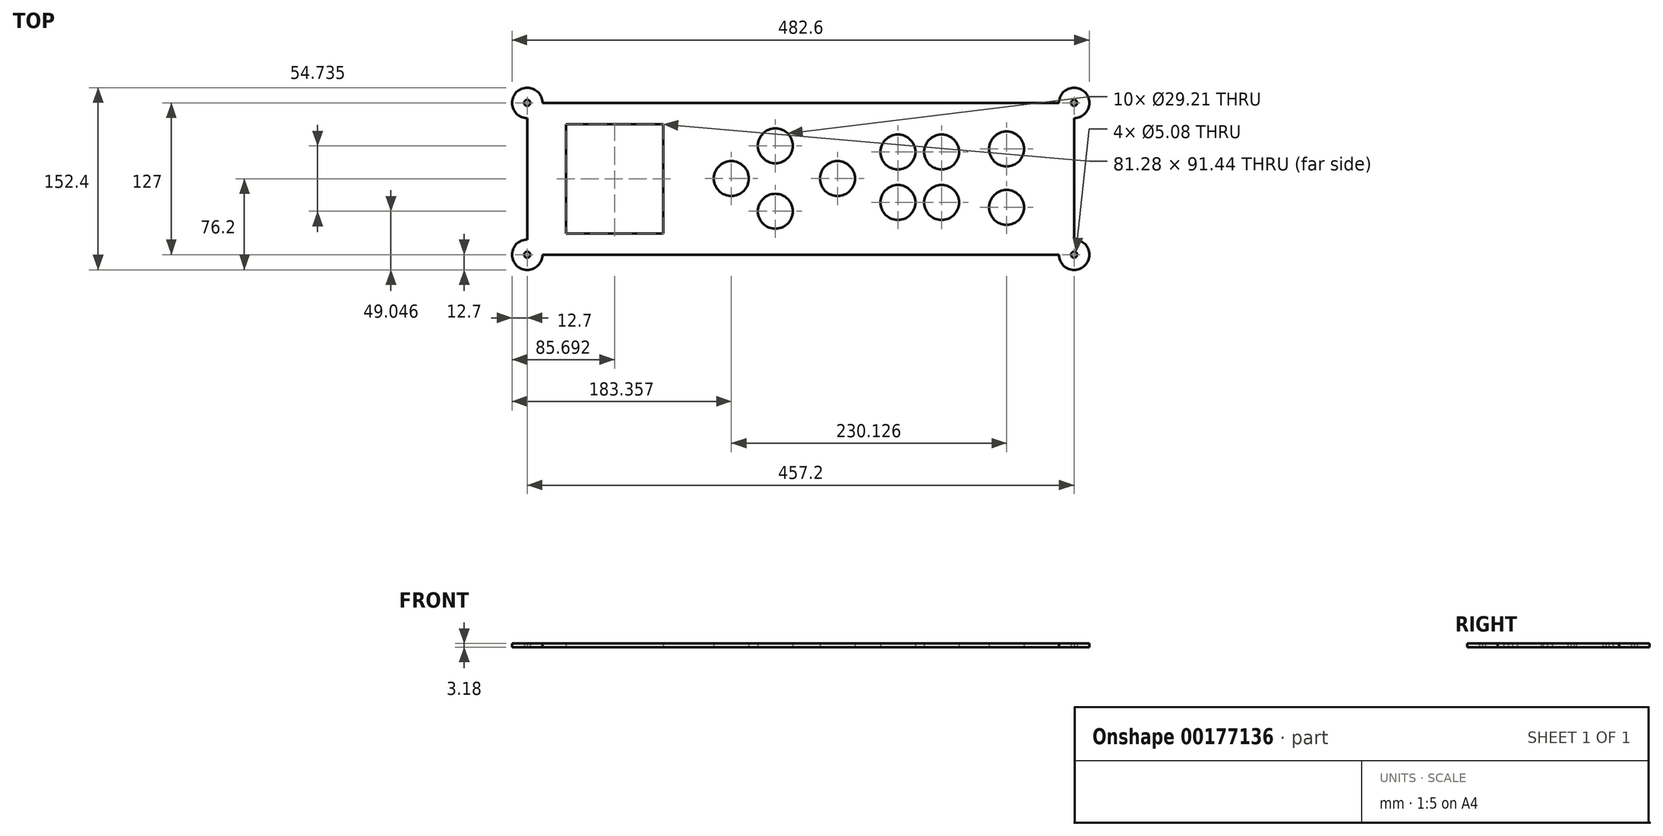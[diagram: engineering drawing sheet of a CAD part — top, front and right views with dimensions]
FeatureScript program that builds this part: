
annotation { "Feature Type Name" : "Feature", "Feature Type Description" : "" }
export const myFeature = defineFeature(function(context is Context, id is Id, definition is map)
    precondition{}
    {
        {
            var Q0;
            Q0=qCreatedBy(makeId("Top.planeOp"),FACE);
            var sketch = newSketch(context, id + "F0", { "sketchPlane" : qUnion([Q0])});
            skLineSegment(sketch, "E0.bottom", {"start": v(12.7, 0) * mm, "end": v(444.5, 0) * mm});
            skLineSegment(sketch, "E0.top", {"start": v(12.7, 127) * mm, "end": v(444.5, 127) * mm});
            skLineSegment(sketch, "E0.left", {"start": v(0, 12.7) * mm, "end": v(0, 114.3) * mm});
            skLineSegment(sketch, "E0.right", {"start": v(457.2, 12.7) * mm, "end": v(457.2, 114.3) * mm});
            skLineSegment(sketch, "E1.bottom", {"start": v(32.35, 109.22) * mm, "end": v(113.63, 109.22) * mm});
            skLineSegment(sketch, "E1.top", {"start": v(32.35, 17.78) * mm, "end": v(113.63, 17.78) * mm});
            skLineSegment(sketch, "E1.left", {"start": v(32.35, 109.22) * mm, "end": v(32.35, 17.78) * mm});
            skLineSegment(sketch, "E1.right", {"start": v(113.63, 109.22) * mm, "end": v(113.63, 17.78) * mm});
            skCircle(sketch, "E2", {"center": v(207.43, 91.08) * mm, "radius": 14.6 * mm});
            skCircle(sketch, "E3", {"center": v(207.43, 36.35) * mm, "radius": 14.6 * mm});
            skCircle(sketch, "E4", {"center": v(170.66, 63.71) * mm, "radius": 14.6 * mm});
            skCircle(sketch, "E5", {"center": v(259.47, 63.71) * mm, "radius": 14.6 * mm});
            skCircle(sketch, "E6", {"center": v(400.78, 88.5) * mm, "radius": 14.6 * mm});
            skCircle(sketch, "E7", {"center": v(400.78, 39.57) * mm, "radius": 14.6 * mm});
            skCircle(sketch, "E8", {"center": v(346.48, 43.68) * mm, "radius": 14.6 * mm});
            skCircle(sketch, "E9", {"center": v(309.94, 43.68) * mm, "radius": 14.6 * mm});
            skCircle(sketch, "E10", {"center": v(309.94, 85.95) * mm, "radius": 14.6 * mm});
            skCircle(sketch, "E11", {"center": v(346.48, 85.95) * mm, "radius": 14.6 * mm});
            skArc(sketch, "E12", {"start": v(457.2, 114.3) * mm, "mid": v(466.18, 135.98) * mm, "end": v(444.5, 127) * mm});
            skArc(sketch, "E13", {"start": v(444.5, 0) * mm, "mid": v(466.18, -8.98) * mm, "end": v(457.2, 12.7) * mm});
            skArc(sketch, "E14", {"start": v(0, 12.7) * mm, "mid": v(-8.98, -8.98) * mm, "end": v(12.7, 0) * mm});
            skArc(sketch, "E15", {"start": v(12.7, 127) * mm, "mid": v(-8.98, 135.98) * mm, "end": v(0, 114.3) * mm});
            skCircle(sketch, "E16", {"center": v(0, 127) * mm, "radius": 2.54 * mm});
            skCircle(sketch, "E17", {"center": v(0, 0) * mm, "radius": 2.54 * mm});
            skCircle(sketch, "E18", {"center": v(457.2, 127) * mm, "radius": 2.54 * mm});
            skCircle(sketch, "E19", {"center": v(457.2, 0) * mm, "radius": 2.54 * mm});
            skLineSegment(sketch, "E20", {"start": v(309.94, 85.95) * mm, "end": v(346.48, 85.95) * mm, "construction": true});
            skLineSegment(sketch, "E21", {"start": v(309.94, 43.68) * mm, "end": v(346.48, 43.68) * mm, "construction": true});
            skLineSegment(sketch, "E22", {"start": v(309.94, 85.95) * mm, "end": v(309.94, 43.68) * mm, "construction": true});
            skLineSegment(sketch, "E23", {"start": v(346.48, 85.95) * mm, "end": v(346.48, 43.68) * mm, "construction": true});
            skLineSegment(sketch, "E24", {"start": v(400.78, 88.5) * mm, "end": v(400.78, 39.57) * mm, "construction": true});
            skLineSegment(sketch, "E25", {"start": v(207.43, 91.08) * mm, "end": v(207.43, 36.35) * mm, "construction": true});
            skLineSegment(sketch, "E26", {"start": v(170.66, 63.71) * mm, "end": v(259.47, 63.71) * mm, "construction": true});
            skLineSegment(sketch, "E27", {"start": v(207.43, 36.35) * mm, "end": v(170.66, 63.71) * mm, "construction": true});
            skLineSegment(sketch, "E28", {"start": v(207.43, 91.08) * mm, "end": v(170.66, 63.71) * mm, "construction": true});
            skSolve(sketch);
        }
        {
            var Q0;
            Q0=makeQuery(id+"F0.imprint","IMPRINT",FACE,{"disambiguationData":[TD([[makeQuery(id+"F0.imprint","IMPRINT",EDGE,{"derivedFrom":sQuery(id+"F0.wireOp",EDGE,"E0.bottom")}),1.0]])]});
            extrude(context, id + "F1", {"entities" : qUnion([Q0]), "depth" : 3.17 * mm});
        }
    });
